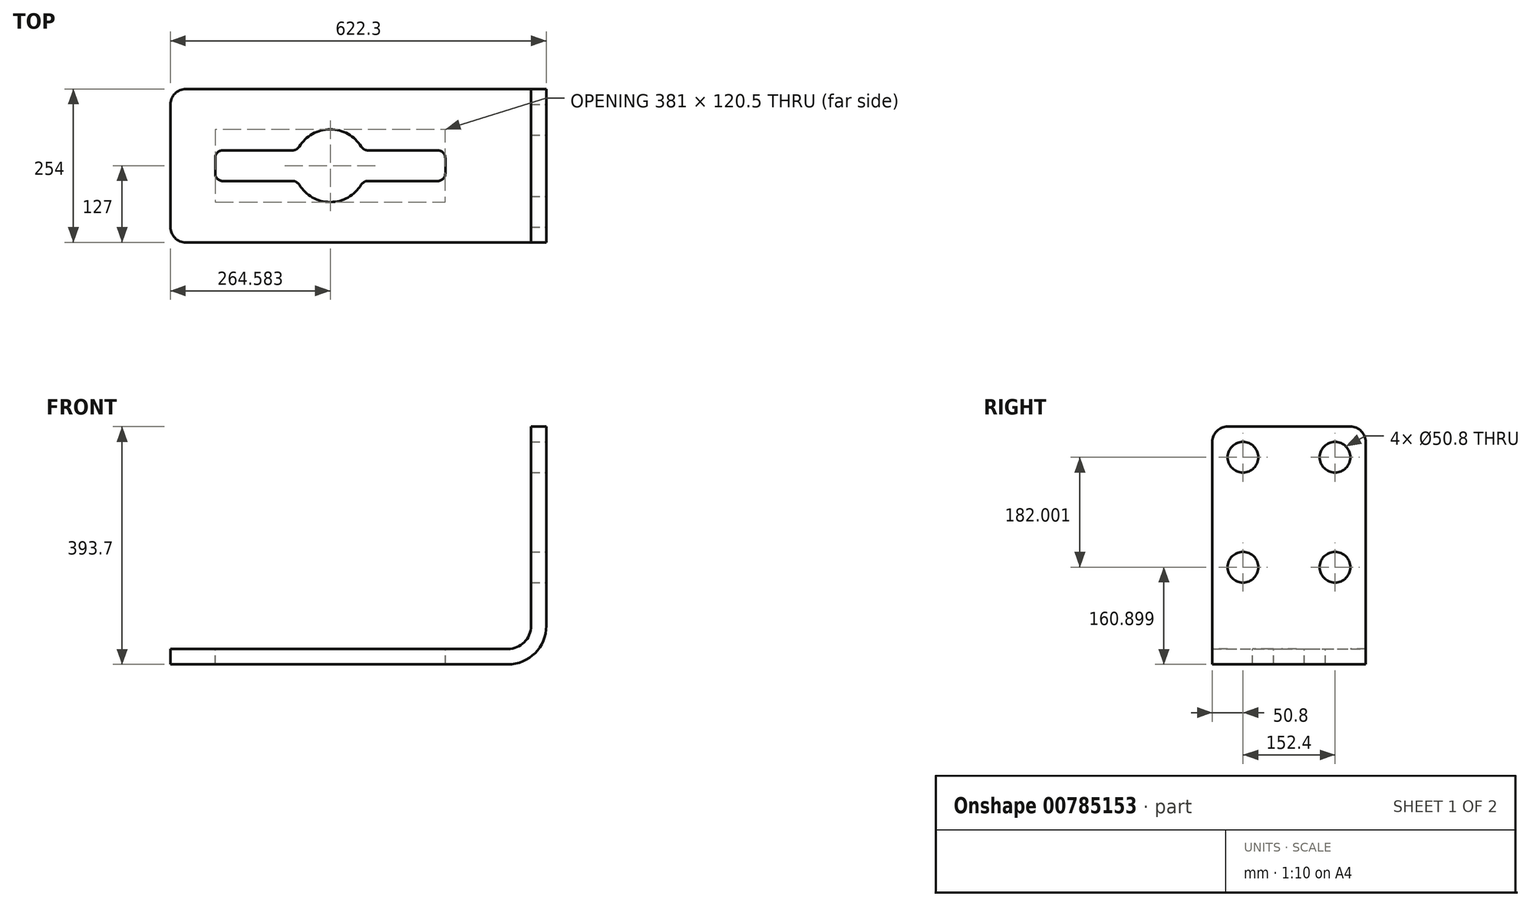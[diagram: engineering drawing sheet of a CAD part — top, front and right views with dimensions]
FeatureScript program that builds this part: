
annotation { "Feature Type Name" : "Feature", "Feature Type Description" : "" }
export const myFeature = defineFeature(function(context is Context, id is Id, definition is map)
    precondition{}
    {
        {
            var Q0;
            Q0=qCreatedBy(makeId("Front.planeOp"),FACE);
            var sketch = newSketch(context, id + "F0", { "sketchPlane" : qUnion([Q0])});
            skArc(sketch, "E0", {"start": v(0, -63.5) * mm, "mid": v(44.9, -44.9) * mm, "end": v(63.5, 0) * mm});
            skLineSegment(sketch, "E1", {"start": v(63.5, 0) * mm, "end": v(63.5, 330.2) * mm});
            skLineSegment(sketch, "E2", {"start": v(63.5, 330.2) * mm, "end": v(38.1, 330.2) * mm});
            skLineSegment(sketch, "E3", {"start": v(38.1, 330.2) * mm, "end": v(38.1, 0) * mm});
            skLineSegment(sketch, "E4", {"start": v(0, -63.5) * mm, "end": v(-558.8, -63.5) * mm});
            skLineSegment(sketch, "E5", {"start": v(-558.8, -63.5) * mm, "end": v(-558.8, -38.1) * mm});
            skLineSegment(sketch, "E6", {"start": v(-558.8, -38.1) * mm, "end": v(0, -38.1) * mm});
            skArc(sketch, "E7", {"start": v(0, -38.1) * mm, "mid": v(26.94, -26.94) * mm, "end": v(38.1, 0) * mm});
            skSolve(sketch);
        }
        {
            var Q0;
            Q0 = qSketchRegion(id + "F0", true);
            extrude(context, id + "F1", {"entities" : qUnion([Q0]), "depth" : 254 * mm, "offsetDistance" : 25.4 * mm});
        }
        {
            var Q0;
            Q0=makeQuery(id+"F1.opExtrude","CAP_EDGE",EDGE,{"disambiguationData":[OSD([sQuery(id+"F0.wireOp",EDGE,"E2")])],"isStart":true});
            var Q1;
            Q1=makeQuery(id+"F1.opExtrude","CAP_EDGE",EDGE,{"disambiguationData":[OSD([sQuery(id+"F0.wireOp",EDGE,"E2")])],"isStart":false});
            var Q2;
            Q2=makeQuery(id+"F1.opExtrude","CAP_EDGE",EDGE,{"disambiguationData":[OSD([sQuery(id+"F0.wireOp",EDGE,"E5")])],"isStart":true});
            var Q3;
            Q3=makeQuery(id+"F1.opExtrude","CAP_EDGE",EDGE,{"disambiguationData":[OSD([sQuery(id+"F0.wireOp",EDGE,"E5")])],"isStart":false});
            fillet(context, id + "F2", {"entities" : qUnion([Q0, Q1, Q2, Q3]), "radius" : 25.4 * mm, "tangentPropagation" : true, "allowEdgeOverflow" : false});
        }
        {
            var Q0;
            Q0=makeQuery(id+"F1.opExtrude","SWEPT_FACE",FACE,{"disambiguationData":[OSD([sQuery(id+"F0.wireOp",EDGE,"E6")])]});
            var sketch = newSketch(context, id + "F3", { "sketchPlane" : qUnion([Q0])});
            skLineSegment(sketch, "E8.bottom", {"start": v(-484.72, -101.6) * mm, "end": v(-103.72, -101.6) * mm});
            skLineSegment(sketch, "E8.top", {"start": v(-484.72, -152.4) * mm, "end": v(-103.72, -152.4) * mm});
            skLineSegment(sketch, "E8.left", {"start": v(-484.72, -101.6) * mm, "end": v(-484.72, -152.4) * mm});
            skLineSegment(sketch, "E8.right", {"start": v(-103.72, -101.6) * mm, "end": v(-103.72, -152.4) * mm});
            skCircle(sketch, "E9", {"center": v(-294.22, -127) * mm, "radius": 60.25 * mm});
            skSolve(sketch);
        }
        {
            var Q0;
            Q0 = qSketchRegion(id + "F3", true);
            extrude(context, id + "F4", {"entities" : qUnion([Q0]), "operationType" : NewBodyOperationType.REMOVE, "oppositeDirection" : true, "depth" : 25.4 * mm, "offsetDistance" : 25.4 * mm});
        }
        {
            var Q0;
            Q0=makeQuery(id+"F4.boolean.opBoolean","COPY",EDGE,{"derivedFrom":makeQuery(id+"F4.opExtrude","SWEPT_EDGE",EDGE,{"disambiguationData":[OSD([sQuery(id+"F3.wireOp",EDGE,"E8.bottom"),sQuery(id+"F3.wireOp",EDGE,"E8.left")])]})});
            var Q1;
            {var subQ0=sQuery(id+"F3.wireOp",EDGE,"E9");var subQ1=sQuery(id+"F3.wireOp",EDGE,"E8.bottom");Q1=makeQuery(id+"F4.boolean.opBoolean","COPY",EDGE,{"derivedFrom":makeQuery(id+"F4.opExtrude","SWEPT_EDGE",EDGE,{"disambiguationData":[OSD([subQ1,subQ0]),TDD([makeQuery(id+"F3.imprint","INTERSECT",VERTEX,{"disambiguationData":[OD(0.0)],"derivedFrom":[subQ1,subQ0]})])]})});}
            var Q2;
            Q2=makeQuery(id+"F4.boolean.opBoolean","COPY",EDGE,{"derivedFrom":makeQuery(id+"F4.opExtrude","SWEPT_EDGE",EDGE,{"disambiguationData":[OSD([sQuery(id+"F3.wireOp",EDGE,"E8.top"),sQuery(id+"F3.wireOp",EDGE,"E8.left")])]})});
            var Q3;
            {var subQ0=sQuery(id+"F3.wireOp",EDGE,"E9");var subQ1=sQuery(id+"F3.wireOp",EDGE,"E8.top");Q3=makeQuery(id+"F4.boolean.opBoolean","COPY",EDGE,{"derivedFrom":makeQuery(id+"F4.opExtrude","SWEPT_EDGE",EDGE,{"disambiguationData":[OSD([subQ1,subQ0]),TDD([makeQuery(id+"F3.imprint","INTERSECT",VERTEX,{"disambiguationData":[OD(0.0)],"derivedFrom":[subQ1,subQ0]})])]})});}
            var Q4;
            {var subQ0=sQuery(id+"F3.wireOp",EDGE,"E9");var subQ1=sQuery(id+"F3.wireOp",EDGE,"E8.top");Q4=makeQuery(id+"F4.boolean.opBoolean","COPY",EDGE,{"derivedFrom":makeQuery(id+"F4.opExtrude","SWEPT_EDGE",EDGE,{"disambiguationData":[OSD([subQ1,subQ0]),TDD([makeQuery(id+"F3.imprint","INTERSECT",VERTEX,{"disambiguationData":[OD(1.0)],"derivedFrom":[subQ1,subQ0]})])]})});}
            var Q5;
            {var subQ0=sQuery(id+"F3.wireOp",EDGE,"E9");var subQ1=sQuery(id+"F3.wireOp",EDGE,"E8.bottom");Q5=makeQuery(id+"F4.boolean.opBoolean","COPY",EDGE,{"derivedFrom":makeQuery(id+"F4.opExtrude","SWEPT_EDGE",EDGE,{"disambiguationData":[OSD([subQ1,subQ0]),TDD([makeQuery(id+"F3.imprint","INTERSECT",VERTEX,{"disambiguationData":[OD(1.0)],"derivedFrom":[subQ1,subQ0]})])]})});}
            var Q6;
            Q6=makeQuery(id+"F4.boolean.opBoolean","COPY",EDGE,{"derivedFrom":makeQuery(id+"F4.opExtrude","SWEPT_EDGE",EDGE,{"disambiguationData":[OSD([sQuery(id+"F3.wireOp",EDGE,"E8.top"),sQuery(id+"F3.wireOp",EDGE,"E8.right")])]})});
            var Q7;
            Q7=makeQuery(id+"F4.boolean.opBoolean","COPY",EDGE,{"derivedFrom":makeQuery(id+"F4.opExtrude","SWEPT_EDGE",EDGE,{"disambiguationData":[OSD([sQuery(id+"F3.wireOp",EDGE,"E8.bottom"),sQuery(id+"F3.wireOp",EDGE,"E8.right")])]})});
            fillet(context, id + "F5", {"entities" : qUnion([Q0, Q1, Q2, Q3, Q4, Q5, Q6, Q7]), "radius" : 12.7 * mm, "tangentPropagation" : true, "allowEdgeOverflow" : false});
        }
        {
            var Q0;
            Q0=makeQuery(id+"F1.opExtrude","SWEPT_FACE",FACE,{"disambiguationData":[OSD([sQuery(id+"F0.wireOp",EDGE,"E1")])]});
            var sketch = newSketch(context, id + "F6", { "sketchPlane" : qUnion([Q0])});
            skCircle(sketch, "E10", {"center": v(-50.8, 279.4) * mm, "radius": 25.4 * mm});
            skCircle(sketch, "E11", {"center": v(-203.2, 279.4) * mm, "radius": 25.4 * mm});
            skCircle(sketch, "E12", {"center": v(-50.8, 97.4) * mm, "radius": 25.4 * mm});
            skCircle(sketch, "E13", {"center": v(-203.2, 97.4) * mm, "radius": 25.4 * mm});
            skSolve(sketch);
        }
        {
            var Q0;
            Q0 = qSketchRegion(id + "F6", true);
            extrude(context, id + "F7", {"entities" : qUnion([Q0]), "operationType" : NewBodyOperationType.REMOVE, "oppositeDirection" : true, "depth" : 25.4 * mm, "offsetDistance" : 25.4 * mm});
        }
    });
